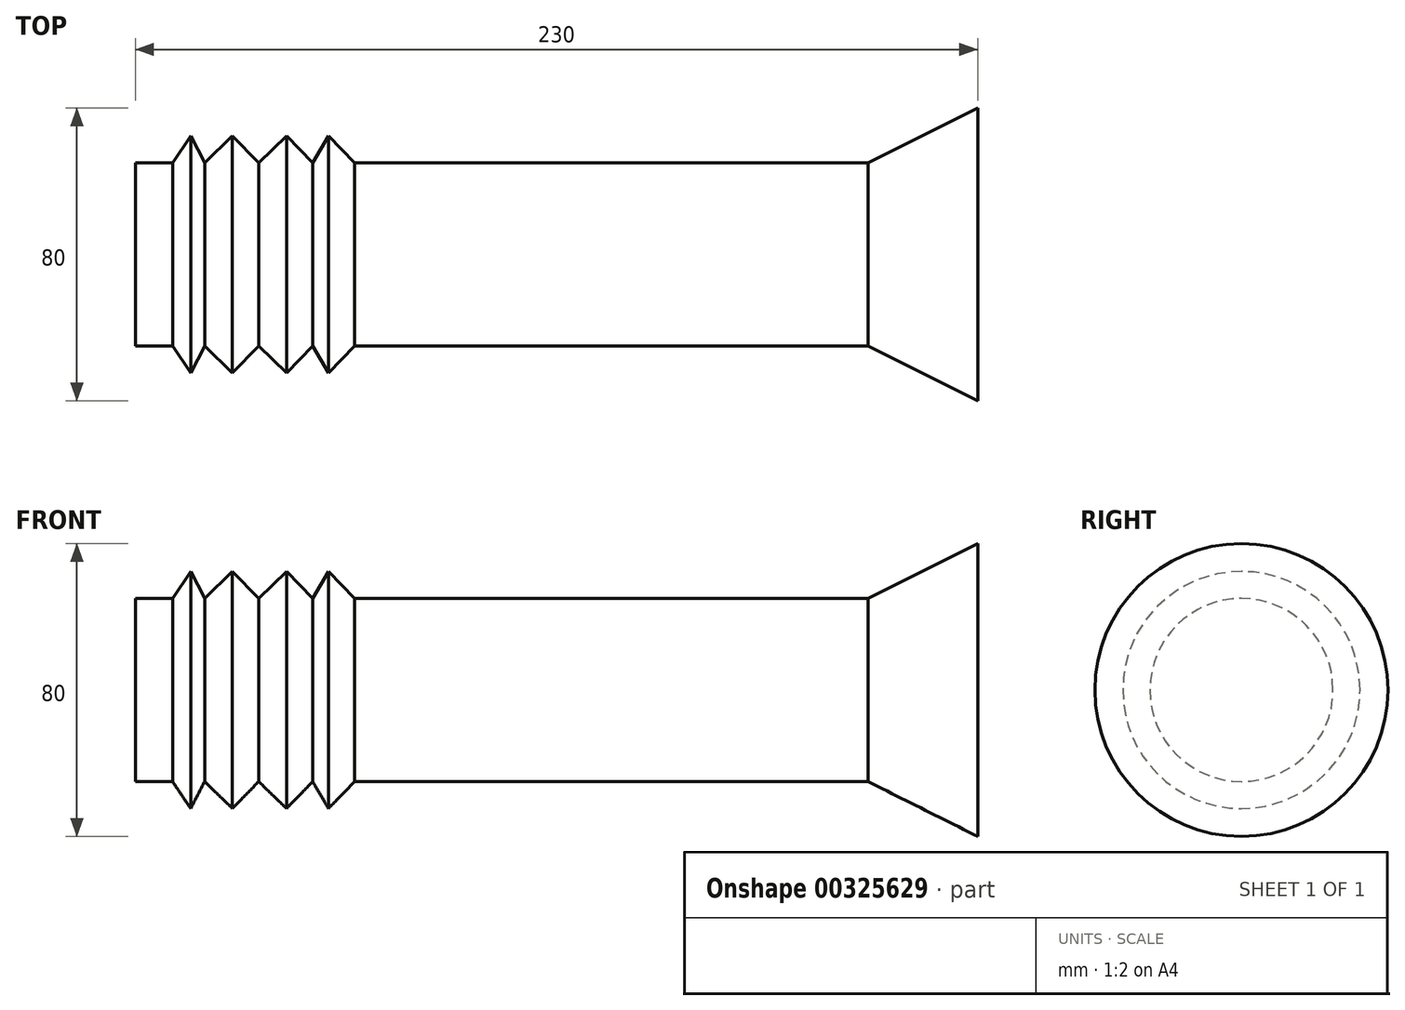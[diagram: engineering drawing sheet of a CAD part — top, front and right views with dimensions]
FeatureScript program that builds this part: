
annotation { "Feature Type Name" : "Feature", "Feature Type Description" : "" }
export const myFeature = defineFeature(function(context is Context, id is Id, definition is map)
    precondition{}
    {
        {
            var Q0;
            Q0=qCreatedBy(makeId("Front.planeOp"),FACE);
            var sketch = newSketch(context, id + "F0", { "sketchPlane" : qUnion([Q0])});
            skLineSegment(sketch, "E0", {"start": v(0, 25) * mm, "end": v(200, 25) * mm});
            skLineSegment(sketch, "E1", {"start": v(200, 25) * mm, "end": v(230, 40) * mm});
            skLineSegment(sketch, "E2", {"start": v(230, 40) * mm, "end": v(230, 0) * mm});
            skLineSegment(sketch, "E3", {"start": v(230, 0) * mm, "end": v(0, 0) * mm});
            skLineSegment(sketch, "E4", {"start": v(0, 0) * mm, "end": v(0, 25) * mm});
            skLineSegment(sketch, "E5", {"start": v(10.16, 25) * mm, "end": v(15.1, 32.38) * mm});
            skLineSegment(sketch, "E6", {"start": v(15.1, 32.38) * mm, "end": v(18.9, 25) * mm});
            skLineSegment(sketch, "E7", {"start": v(18.9, 25) * mm, "end": v(26.5, 32.38) * mm});
            skLineSegment(sketch, "E8", {"start": v(26.5, 32.38) * mm, "end": v(33.66, 25) * mm});
            skLineSegment(sketch, "E9", {"start": v(33.66, 25) * mm, "end": v(41.26, 32.38) * mm});
            skLineSegment(sketch, "E10", {"start": v(41.26, 32.38) * mm, "end": v(48.43, 25) * mm});
            skLineSegment(sketch, "E11", {"start": v(48.43, 25) * mm, "end": v(52.72, 32.38) * mm});
            skLineSegment(sketch, "E12", {"start": v(52.72, 32.38) * mm, "end": v(59.88, 25) * mm});
            skSolve(sketch);
        }
        {
            var Q0;
            Q0 = qSketchRegion(id + "F0", true);
            var Q1;
            Q1=sQuery(id+"F0.wireOp",EDGE,"E3");
            revolve(context, id + "F1", {"entities" : qUnion([Q0]), "axis" : qUnion([Q1]), "revolveType" : RevolveType.FULL});
        }
    });
